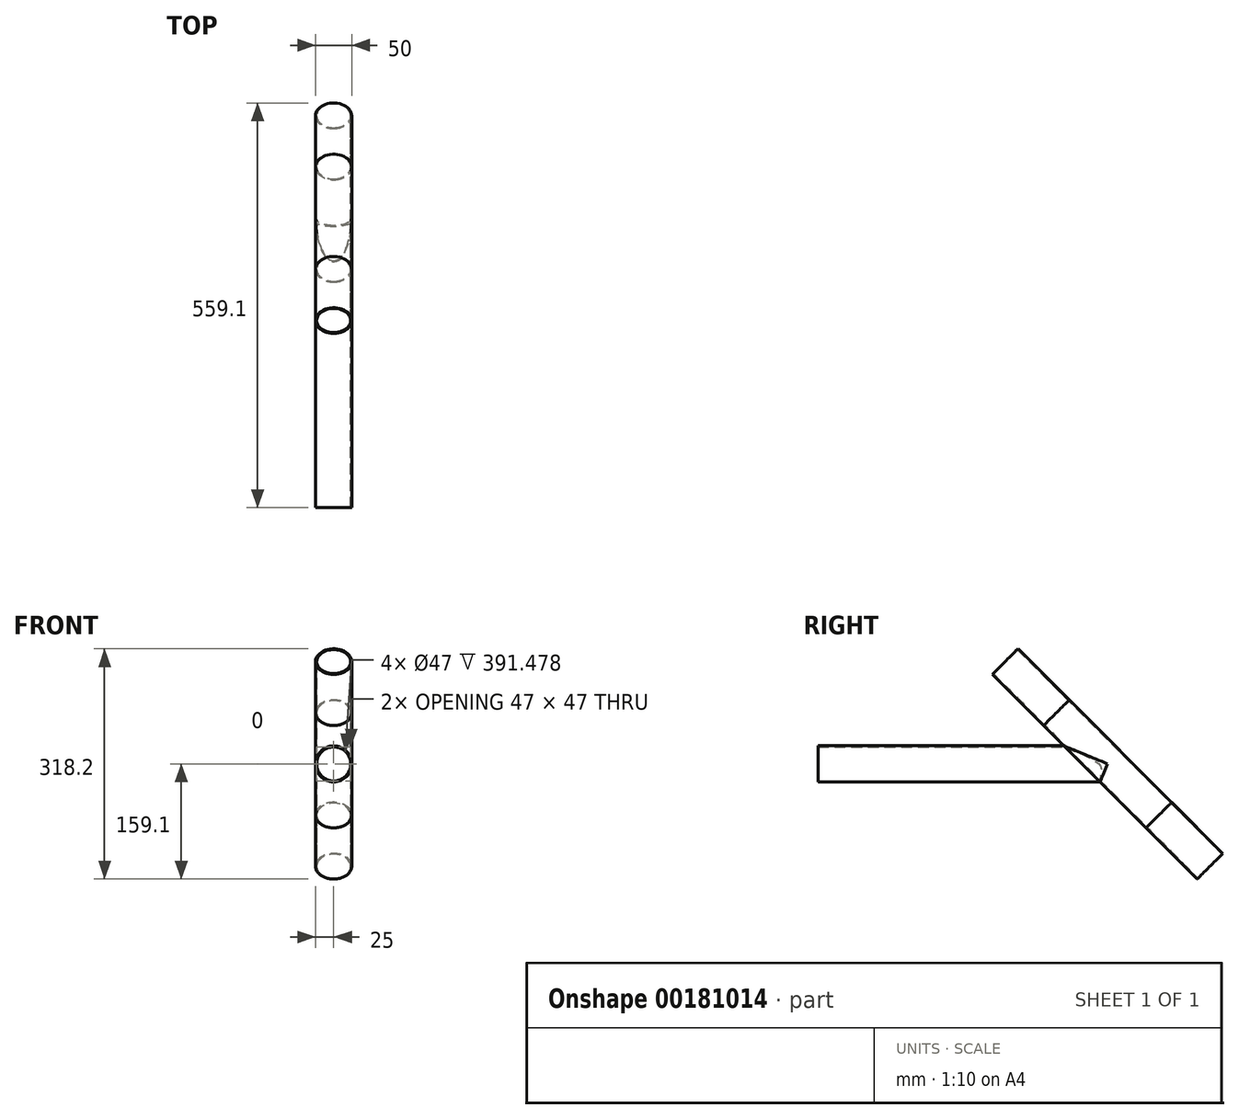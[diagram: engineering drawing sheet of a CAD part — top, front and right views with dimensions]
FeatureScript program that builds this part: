
annotation { "Feature Type Name" : "Feature", "Feature Type Description" : "" }
export const myFeature = defineFeature(function(context is Context, id is Id, definition is map)
    precondition{}
    {
        {
            var Q0;
            Q0=qCreatedBy(makeId("Front.planeOp"),FACE);
            var sketch = newSketch(context, id + "F0", { "sketchPlane" : qUnion([Q0])});
            skCircle(sketch, "E0", {"center": v(0, 0) * mm, "radius": 25 * mm});
            skCircle(sketch, "E1", {"center": v(0, 0) * mm, "radius": 23.5 * mm});
            skLineSegment(sketch, "E2", {"start": v(31.9, 0) * mm, "end": v(-42.1, 0) * mm, "construction": true});
            skSolve(sketch);
        }
        {
            var Q0;
            Q0 = qSketchRegion(id + "F0", true);
            extrude(context, id + "F1", {"entities" : qUnion([Q0]), "depth" : 400 * mm});
        }
        {
            var Q0;
            Q0=sQuery(id+"F0.wireOp",EDGE,"E2");
            cPlane(context, id + "F2", {"entities" : qUnion([Q0]), "cplaneType" : CPlaneType.LINE_ANGLE, "offset" : 25 * mm, "angle" : 45 * degree, "width" : 150 * mm, "height" : 150 * mm});
        }
        {
            var Q0;
            Q0=qCreatedBy(id+"F2.planeOp",FACE);
            var sketch = newSketch(context, id + "F3", { "sketchPlane" : qUnion([Q0])});
            skCircle(sketch, "E3", {"center": v(0, 0) * mm, "radius": 25 * mm});
            skCircle(sketch, "E4", {"center": v(0, 0) * mm, "radius": 23.5 * mm});
            skSolve(sketch);
        }
        {
            var Q0;
            Q0=makeQuery(id+"F3.imprint","IMPRINT",FACE,{"disambiguationData":[TD([[makeQuery(id+"F3.imprint","IMPRINT",EDGE,{"derivedFrom":sQuery(id+"F3.wireOp",EDGE,"E3")}),1.0]])]});
            var Q1;
            Q1=makeQuery(id+"F3.imprint","IMPRINT",FACE,{"disambiguationData":[TD([[makeQuery(id+"F3.imprint","IMPRINT",EDGE,{"derivedFrom":sQuery(id+"F3.wireOp",EDGE,"E4")}),1.0]])]});
            extrude(context, id + "F4", {"entities" : qUnion([Q0, Q1]), "operationType" : NewBodyOperationType.REMOVE, "endBound" : BoundingType.SYMMETRIC, "depth" : 200 * mm});
        }
        {
            var Q0;
            Q0=makeQuery(id+"F3.imprint","IMPRINT",FACE,{"disambiguationData":[TD([[makeQuery(id+"F3.imprint","IMPRINT",EDGE,{"derivedFrom":sQuery(id+"F3.wireOp",EDGE,"E3")}),1.0]])]});
            extrude(context, id + "F5", {"entities" : qUnion([Q0]), "endBound" : BoundingType.SYMMETRIC, "depth" : 400 * mm});
        }
    });
